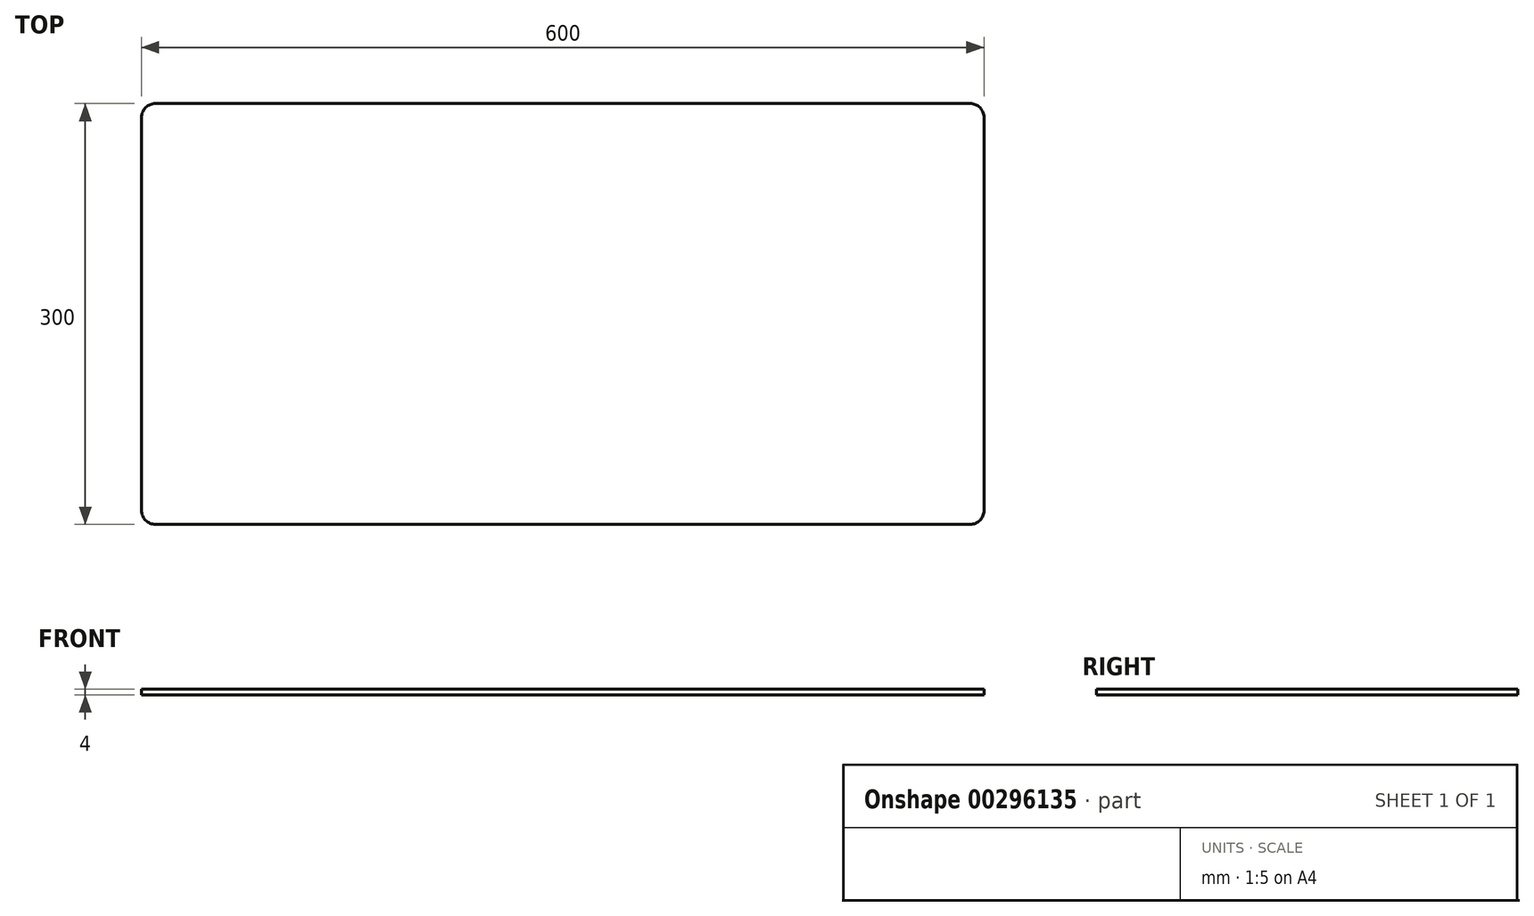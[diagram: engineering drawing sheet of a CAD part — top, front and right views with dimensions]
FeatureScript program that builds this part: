
annotation { "Feature Type Name" : "Feature", "Feature Type Description" : "" }
export const myFeature = defineFeature(function(context is Context, id is Id, definition is map)
    precondition{}
    {
        {
            var Q0;
            Q0=qCreatedBy(makeId("Top.planeOp"),FACE);
            var sketch = newSketch(context, id + "F0", { "sketchPlane" : qUnion([Q0])});
            skLineSegment(sketch, "E0.bottom", {"start": v(-290, 150) * mm, "end": v(290, 150) * mm});
            skLineSegment(sketch, "E0.top", {"start": v(-290, -150) * mm, "end": v(290, -150) * mm});
            skLineSegment(sketch, "E0.left", {"start": v(-300, 140) * mm, "end": v(-300, -140) * mm});
            skLineSegment(sketch, "E0.right", {"start": v(300, 140) * mm, "end": v(300, -140) * mm});
            skPoint(sketch, "E0.middle", {"position": v(0, 0) * mm});
            skPoint(sketch, "E1.visualSharp", {"position": v(-300, -150) * mm});
            skArc(sketch, "E1.filletArc", {"start": v(-300, -140) * mm, "mid": v(-297.07, -147.07) * mm, "end": v(-290, -150) * mm});
            skPoint(sketch, "E2.visualSharp", {"position": v(-300, 150) * mm});
            skArc(sketch, "E2.filletArc", {"start": v(-290, 150) * mm, "mid": v(-297.07, 147.07) * mm, "end": v(-300, 140) * mm});
            skPoint(sketch, "E3.visualSharp", {"position": v(300, 150) * mm});
            skArc(sketch, "E3.filletArc", {"start": v(300, 140) * mm, "mid": v(297.07, 147.07) * mm, "end": v(290, 150) * mm});
            skPoint(sketch, "E4.visualSharp", {"position": v(300, -150) * mm});
            skArc(sketch, "E4.filletArc", {"start": v(290, -150) * mm, "mid": v(297.07, -147.07) * mm, "end": v(300, -140) * mm});
            skSolve(sketch);
        }
        {
            var Q0;
            Q0=qSketchRegion(id+"F0",true);
            extrude(context, id + "F1", {"entities" : qUnion([Q0]), "oppositeDirection" : true, "depth" : 4 * mm});
        }
    });
